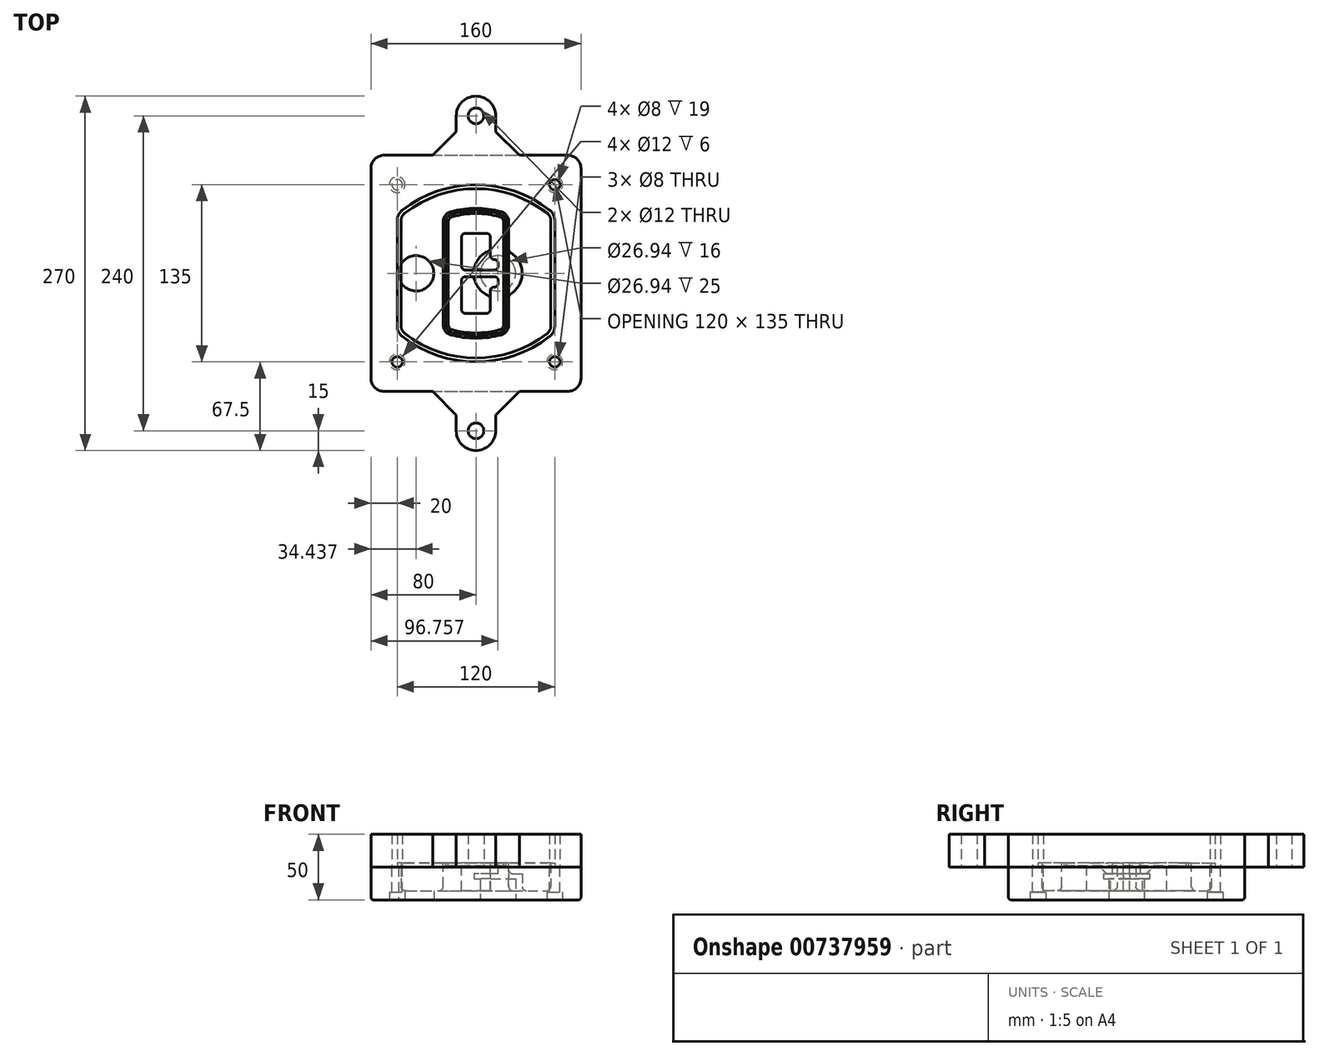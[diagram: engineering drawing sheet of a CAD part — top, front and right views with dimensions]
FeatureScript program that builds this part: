
annotation { "Feature Type Name" : "Feature", "Feature Type Description" : "" }
export const myFeature = defineFeature(function(context is Context, id is Id, definition is map)
    precondition{}
    {
        {
            var Q0;
            Q0=qCreatedBy(makeId("Top.planeOp"),FACE);
            var sketch = newSketch(context, id + "F0", { "sketchPlane" : qUnion([Q0])});
            skPoint(sketch, "E0.rect.middle", {"position": v(0, 0) * mm});
            skLineSegment(sketch, "E1.bottom", {"start": v(-70, -90) * mm, "end": v(70, -90) * mm});
            skLineSegment(sketch, "E1.top", {"start": v(-70, 90) * mm, "end": v(70, 90) * mm});
            skLineSegment(sketch, "E1.left", {"start": v(-80, -80) * mm, "end": v(-80, 80) * mm});
            skLineSegment(sketch, "E1.right", {"start": v(80, -80) * mm, "end": v(80, 80) * mm});
            skLineSegment(sketch, "E2", {"start": v(-80, 90) * mm, "end": v(80, -90) * mm, "construction": true});
            skLineSegment(sketch, "E3", {"start": v(80, 90) * mm, "end": v(-80, -90) * mm, "construction": true});
            skCircle(sketch, "E4", {"center": v(-60, 67.5) * mm, "radius": 4 * mm});
            skCircle(sketch, "E5", {"center": v(60, 67.5) * mm, "radius": 4 * mm});
            skCircle(sketch, "E6", {"center": v(60, -67.5) * mm, "radius": 4 * mm});
            skCircle(sketch, "E7", {"center": v(-60, -67.5) * mm, "radius": 4 * mm});
            skLineSegment(sketch, "E8", {"start": v(-60, 67.5) * mm, "end": v(60, 67.5) * mm, "construction": true});
            skLineSegment(sketch, "E9", {"start": v(60, 67.5) * mm, "end": v(60, -67.5) * mm, "construction": true});
            skLineSegment(sketch, "E10", {"start": v(60, -67.5) * mm, "end": v(-60, -67.5) * mm, "construction": true});
            skLineSegment(sketch, "E11", {"start": v(-60, -67.5) * mm, "end": v(-60, 67.5) * mm, "construction": true});
            skLineSegment(sketch, "E12", {"start": v(-60, 40.3) * mm, "end": v(-60, -40.3) * mm});
            skLineSegment(sketch, "E13", {"start": v(60, 40.3) * mm, "end": v(60, -40.3) * mm});
            skArc(sketch, "E14", {"start": v(56.15, 48.18) * mm, "mid": v(0, 67.5) * mm, "end": v(-56.15, 48.18) * mm});
            skArc(sketch, "E15", {"start": v(-56.15, -48.18) * mm, "mid": v(0, -67.5) * mm, "end": v(56.15, -48.18) * mm});
            skLineSegment(sketch, "E16", {"start": v(-60, 0) * mm, "end": v(60, 0) * mm, "construction": true});
            skPoint(sketch, "E17.visualSharp", {"position": v(-60, -45) * mm});
            skArc(sketch, "E17.filletArc", {"start": v(-60, -40.3) * mm, "mid": v(-58.99, -44.68) * mm, "end": v(-56.15, -48.18) * mm});
            skPoint(sketch, "E18.visualSharp", {"position": v(-60, 45) * mm});
            skArc(sketch, "E18.filletArc", {"start": v(-56.15, 48.18) * mm, "mid": v(-58.99, 44.68) * mm, "end": v(-60, 40.3) * mm});
            skPoint(sketch, "E19.visualSharp", {"position": v(60, 45) * mm});
            skArc(sketch, "E19.filletArc", {"start": v(60, 40.3) * mm, "mid": v(58.99, 44.68) * mm, "end": v(56.15, 48.18) * mm});
            skPoint(sketch, "E20.visualSharp", {"position": v(60, -45) * mm});
            skArc(sketch, "E20.filletArc", {"start": v(56.15, -48.18) * mm, "mid": v(58.99, -44.68) * mm, "end": v(60, -40.3) * mm});
            skPoint(sketch, "E21.visualSharp", {"position": v(-80, 90) * mm});
            skArc(sketch, "E21.filletArc", {"start": v(-70, 90) * mm, "mid": v(-77.07, 87.07) * mm, "end": v(-80, 80) * mm});
            skPoint(sketch, "E22.visualSharp", {"position": v(80, 90) * mm});
            skArc(sketch, "E22.filletArc", {"start": v(80, 80) * mm, "mid": v(77.07, 87.07) * mm, "end": v(70, 90) * mm});
            skPoint(sketch, "E23.visualSharp", {"position": v(80, -90) * mm});
            skArc(sketch, "E23.filletArc", {"start": v(70, -90) * mm, "mid": v(77.07, -87.07) * mm, "end": v(80, -80) * mm});
            skPoint(sketch, "E24.visualSharp", {"position": v(-80, -90) * mm});
            skArc(sketch, "E24.filletArc", {"start": v(-80, -80) * mm, "mid": v(-77.07, -87.07) * mm, "end": v(-70, -90) * mm});
            skArc(sketch, "E25.0", {"start": v(57, 40.3) * mm, "mid": v(56.3, 43.36) * mm, "end": v(54.3, 45.81) * mm});
            skLineSegment(sketch, "E25.1", {"start": v(57, 40.3) * mm, "end": v(57, -40.3) * mm});
            skArc(sketch, "E25.2", {"start": v(54.3, -45.81) * mm, "mid": v(56.3, -43.36) * mm, "end": v(57, -40.3) * mm});
            skArc(sketch, "E25.3", {"start": v(-54.3, -45.81) * mm, "mid": v(0, -64.5) * mm, "end": v(54.3, -45.81) * mm});
            skArc(sketch, "E25.4", {"start": v(-57, -40.3) * mm, "mid": v(-56.3, -43.36) * mm, "end": v(-54.3, -45.81) * mm});
            skArc(sketch, "E25.5", {"start": v(54.3, 45.81) * mm, "mid": v(0, 64.5) * mm, "end": v(-54.3, 45.81) * mm});
            skLineSegment(sketch, "E25.6", {"start": v(-57, 40.3) * mm, "end": v(-57, -40.3) * mm});
            skArc(sketch, "E25.7", {"start": v(-54.3, 45.81) * mm, "mid": v(-56.3, 43.36) * mm, "end": v(-57, 40.3) * mm});
            skArc(sketch, "E26.0", {"start": v(-58.62, 51.33) * mm, "mid": v(-62.58, 46.43) * mm, "end": v(-64, 40.3) * mm});
            skArc(sketch, "E26.1", {"start": v(58.62, 51.33) * mm, "mid": v(0, 71.5) * mm, "end": v(-58.62, 51.33) * mm});
            skArc(sketch, "E26.2", {"start": v(64, 40.3) * mm, "mid": v(62.58, 46.43) * mm, "end": v(58.62, 51.33) * mm});
            skLineSegment(sketch, "E26.3", {"start": v(64, 40.3) * mm, "end": v(64, -40.3) * mm});
            skArc(sketch, "E26.4", {"start": v(58.62, -51.33) * mm, "mid": v(62.58, -46.43) * mm, "end": v(64, -40.3) * mm});
            skLineSegment(sketch, "E26.5", {"start": v(-64, 40.3) * mm, "end": v(-64, -40.3) * mm});
            skArc(sketch, "E26.6", {"start": v(-58.62, -51.33) * mm, "mid": v(0, -71.5) * mm, "end": v(58.62, -51.33) * mm});
            skArc(sketch, "E26.7", {"start": v(-64, -40.3) * mm, "mid": v(-62.58, -46.43) * mm, "end": v(-58.62, -51.33) * mm});
            skSolve(sketch);
        }
        {
            var Q0;
            Q0=makeQuery(id+"F0.imprint","IMPRINT",FACE,{"disambiguationData":[TD([[makeQuery(id+"F0.imprint","IMPRINT",EDGE,{"derivedFrom":sQuery(id+"F0.wireOp",EDGE,"E1.bottom")}),1.0]])]});
            var Q1;
            Q1=makeQuery(id+"F0.imprint","IMPRINT",FACE,{"disambiguationData":[TD([[makeQuery(id+"F0.imprint","IMPRINT",EDGE,{"derivedFrom":sQuery(id+"F0.wireOp",EDGE,"E12")}),1.0]])]});
            var Q2;
            Q2=makeQuery(id+"F0.imprint","IMPRINT",FACE,{"disambiguationData":[TD([[makeQuery(id+"F0.imprint","IMPRINT",EDGE,{"derivedFrom":sQuery(id+"F0.wireOp",EDGE,"E25.0")}),1.0]])]});
            var Q3;
            Q3=makeQuery(id+"F0.imprint","IMPRINT",FACE,{"disambiguationData":[TD([[makeQuery(id+"F0.imprint","IMPRINT",EDGE,{"derivedFrom":sQuery(id+"F0.wireOp",EDGE,"E12")}),-1.0]])]});
            extrude(context, id + "F1", {"entities" : qUnion([Q0, Q1, Q2, Q3]), "oppositeDirection" : true, "depth" : 25 * mm});
        }
        {
            var Q0;
            Q0=makeQuery(id+"F0.imprint","IMPRINT",FACE,{"disambiguationData":[TD([[makeQuery(id+"F0.imprint","IMPRINT",EDGE,{"derivedFrom":sQuery(id+"F0.wireOp",EDGE,"E12")}),1.0]])]});
            extrude(context, id + "F2", {"entities" : qUnion([Q0]), "operationType" : NewBodyOperationType.ADD, "depth" : 3 * mm});
        }
        {
            var Q0;
            Q0=makeQuery(id+"F0.imprint","IMPRINT",FACE,{"disambiguationData":[TD([[makeQuery(id+"F0.imprint","IMPRINT",EDGE,{"derivedFrom":sQuery(id+"F0.wireOp",EDGE,"E25.0")}),1.0]])]});
            extrude(context, id + "F3", {"entities" : qUnion([Q0]), "operationType" : NewBodyOperationType.REMOVE, "oppositeDirection" : true, "depth" : 18 * mm});
        }
        {
            var Q0;
            Q0=makeQuery(id+"F2.opExtrude","CAP_FACE",FACE,{"disambiguationData":[OSD([sQuery(id+"F0.wireOp",EDGE,"E12"),sQuery(id+"F0.wireOp",EDGE,"E13"),sQuery(id+"F0.wireOp",EDGE,"E14"),sQuery(id+"F0.wireOp",EDGE,"E15"),sQuery(id+"F0.wireOp",EDGE,"E17.filletArc"),sQuery(id+"F0.wireOp",EDGE,"E18.filletArc"),sQuery(id+"F0.wireOp",EDGE,"E19.filletArc"),sQuery(id+"F0.wireOp",EDGE,"E20.filletArc"),sQuery(id+"F0.wireOp",EDGE,"E25.0"),sQuery(id+"F0.wireOp",EDGE,"E25.1"),sQuery(id+"F0.wireOp",EDGE,"E25.2"),sQuery(id+"F0.wireOp",EDGE,"E25.3"),sQuery(id+"F0.wireOp",EDGE,"E25.4"),sQuery(id+"F0.wireOp",EDGE,"E25.5"),sQuery(id+"F0.wireOp",EDGE,"E25.6"),sQuery(id+"F0.wireOp",EDGE,"E25.7")])],"isStart":false});
            var sketch = newSketch(context, id + "F4", { "sketchPlane" : qUnion([Q0])});
            skArc(sketch, "E27.0", {"start": v(-19.08, -46.97) * mm, "mid": v(0, -49.5) * mm, "end": v(19.08, -46.97) * mm});
            skArc(sketch, "E28.0", {"start": v(19.08, 46.97) * mm, "mid": v(0, 49.5) * mm, "end": v(-19.08, 46.97) * mm});
            skLineSegment(sketch, "E29", {"start": v(-25, 39.25) * mm, "end": v(-25, -39.25) * mm});
            skLineSegment(sketch, "E30", {"start": v(25, 39.25) * mm, "end": v(25, -39.25) * mm});
            skLineSegment(sketch, "E31", {"start": v(-25, 45.1) * mm, "end": v(25, 45.1) * mm, "construction": true});
            skLineSegment(sketch, "E32", {"start": v(-25, -45.1) * mm, "end": v(25, -45.1) * mm, "construction": true});
            skPoint(sketch, "E33.visualSharp", {"position": v(-25, 45.1) * mm});
            skArc(sketch, "E33.filletArc", {"start": v(-19.08, 46.97) * mm, "mid": v(-23.35, 44.11) * mm, "end": v(-25, 39.25) * mm});
            skPoint(sketch, "E34.visualSharp", {"position": v(25, 45.1) * mm});
            skArc(sketch, "E34.filletArc", {"start": v(25, 39.25) * mm, "mid": v(23.35, 44.11) * mm, "end": v(19.08, 46.97) * mm});
            skPoint(sketch, "E35.visualSharp", {"position": v(25, -45.1) * mm});
            skArc(sketch, "E35.filletArc", {"start": v(19.08, -46.97) * mm, "mid": v(23.35, -44.11) * mm, "end": v(25, -39.25) * mm});
            skPoint(sketch, "E36.visualSharp", {"position": v(-25, -45.1) * mm});
            skArc(sketch, "E36.filletArc", {"start": v(-25, -39.25) * mm, "mid": v(-23.35, -44.11) * mm, "end": v(-19.08, -46.97) * mm});
            skArc(sketch, "E37.0", {"start": v(54.3, 45.81) * mm, "mid": v(0, 64.5) * mm, "end": v(-54.3, 45.81) * mm});
            skArc(sketch, "E37.1", {"start": v(-54.3, 45.81) * mm, "mid": v(-56.3, 43.36) * mm, "end": v(-57, 40.3) * mm});
            skLineSegment(sketch, "E37.2", {"start": v(-57, 40.3) * mm, "end": v(-57, -40.3) * mm});
            skArc(sketch, "E37.3", {"start": v(-57, -40.3) * mm, "mid": v(-56.3, -43.36) * mm, "end": v(-54.3, -45.81) * mm});
            skArc(sketch, "E37.4", {"start": v(-54.3, -45.81) * mm, "mid": v(0, -64.5) * mm, "end": v(54.3, -45.81) * mm});
            skArc(sketch, "E37.5", {"start": v(54.3, -45.81) * mm, "mid": v(56.3, -43.36) * mm, "end": v(57, -40.3) * mm});
            skLineSegment(sketch, "E37.6", {"start": v(57, 40.3) * mm, "end": v(57, -40.3) * mm});
            skArc(sketch, "E37.7", {"start": v(57, 40.3) * mm, "mid": v(56.3, 43.36) * mm, "end": v(54.3, 45.81) * mm});
            skLineSegment(sketch, "E38.0", {"start": v(23, 39.25) * mm, "end": v(23, -39.25) * mm});
            skArc(sketch, "E38.1", {"start": v(18.56, -45.04) * mm, "mid": v(21.76, -42.9) * mm, "end": v(23, -39.25) * mm});
            skArc(sketch, "E38.2", {"start": v(-18.56, -45.04) * mm, "mid": v(0, -47.5) * mm, "end": v(18.56, -45.04) * mm});
            skArc(sketch, "E38.3", {"start": v(-23, -39.25) * mm, "mid": v(-21.76, -42.9) * mm, "end": v(-18.56, -45.04) * mm});
            skLineSegment(sketch, "E38.4", {"start": v(-23, 39.25) * mm, "end": v(-23, -39.25) * mm});
            skArc(sketch, "E38.5", {"start": v(23, 39.25) * mm, "mid": v(21.76, 42.9) * mm, "end": v(18.56, 45.04) * mm});
            skArc(sketch, "E38.6", {"start": v(-18.56, 45.04) * mm, "mid": v(-21.76, 42.9) * mm, "end": v(-23, 39.25) * mm});
            skArc(sketch, "E38.7", {"start": v(18.56, 45.04) * mm, "mid": v(0, 47.5) * mm, "end": v(-18.56, 45.04) * mm});
            skArc(sketch, "E39.0", {"start": v(21, 39.25) * mm, "mid": v(20.18, 41.68) * mm, "end": v(18.04, 43.1) * mm});
            skLineSegment(sketch, "E39.1", {"start": v(21, 39.25) * mm, "end": v(21, -39.25) * mm});
            skArc(sketch, "E39.2", {"start": v(18.04, -43.1) * mm, "mid": v(20.18, -41.68) * mm, "end": v(21, -39.25) * mm});
            skArc(sketch, "E39.3", {"start": v(-18.04, -43.1) * mm, "mid": v(0, -45.5) * mm, "end": v(18.04, -43.1) * mm});
            skArc(sketch, "E39.4", {"start": v(-21, -39.25) * mm, "mid": v(-20.18, -41.68) * mm, "end": v(-18.04, -43.1) * mm});
            skArc(sketch, "E39.5", {"start": v(18.04, 43.1) * mm, "mid": v(0, 45.5) * mm, "end": v(-18.04, 43.1) * mm});
            skLineSegment(sketch, "E39.6", {"start": v(-21, 39.25) * mm, "end": v(-21, -39.25) * mm});
            skArc(sketch, "E39.7", {"start": v(-18.04, 43.1) * mm, "mid": v(-20.18, 41.68) * mm, "end": v(-21, 39.25) * mm});
            skLineSegment(sketch, "E40", {"start": v(-25, 0) * mm, "end": v(25, 0) * mm, "construction": true});
            skLineSegment(sketch, "E41", {"start": v(-11, 5.5) * mm, "end": v(-11, 27.5) * mm});
            skLineSegment(sketch, "E42", {"start": v(-8, 30.5) * mm, "end": v(8, 30.5) * mm});
            skLineSegment(sketch, "E43", {"start": v(11, 27.5) * mm, "end": v(11, 13.5) * mm});
            skLineSegment(sketch, "E44", {"start": v(14, 10.5) * mm, "end": v(14, 10.5) * mm});
            skLineSegment(sketch, "E45", {"start": v(17, 7.5) * mm, "end": v(17, 5.5) * mm});
            skLineSegment(sketch, "E46", {"start": v(14, 2.5) * mm, "end": v(-8, 2.5) * mm});
            skPoint(sketch, "E47.visualSharp", {"position": v(-11, 30.5) * mm});
            skArc(sketch, "E47.filletArc", {"start": v(-8, 30.5) * mm, "mid": v(-10.12, 29.62) * mm, "end": v(-11, 27.5) * mm});
            skPoint(sketch, "E48.visualSharp", {"position": v(11, 30.5) * mm});
            skArc(sketch, "E48.filletArc", {"start": v(11, 27.5) * mm, "mid": v(10.12, 29.62) * mm, "end": v(8, 30.5) * mm});
            skPoint(sketch, "E49.visualSharp", {"position": v(11, 10.5) * mm});
            skArc(sketch, "E49.filletArc", {"start": v(11, 13.5) * mm, "mid": v(11.88, 11.38) * mm, "end": v(14, 10.5) * mm});
            skPoint(sketch, "E50.visualSharp", {"position": v(17, 10.5) * mm});
            skArc(sketch, "E50.filletArc", {"start": v(17, 7.5) * mm, "mid": v(16.12, 9.62) * mm, "end": v(14, 10.5) * mm});
            skPoint(sketch, "E51.visualSharp", {"position": v(17, 2.5) * mm});
            skArc(sketch, "E51.filletArc", {"start": v(14, 2.5) * mm, "mid": v(16.12, 3.38) * mm, "end": v(17, 5.5) * mm});
            skPoint(sketch, "E52.visualSharp", {"position": v(-11, 2.5) * mm});
            skArc(sketch, "E52.filletArc", {"start": v(-11, 5.5) * mm, "mid": v(-10.12, 3.38) * mm, "end": v(-8, 2.5) * mm});
            skLineSegment(sketch, "E53.0.MirrorCS", {"start": v(14, -2.5) * mm, "end": v(-8, -2.5) * mm});
            skArc(sketch, "E54.0.MirrorCS", {"start": v(-11, -5.5) * mm, "mid": v(-10.12, -3.38) * mm, "end": v(-8, -2.5) * mm});
            skLineSegment(sketch, "E55.0.MirrorCS", {"start": v(-11, -5.5) * mm, "end": v(-11, -27.5) * mm});
            skArc(sketch, "E56.0.MirrorCS", {"start": v(-8, -30.5) * mm, "mid": v(-10.12, -29.62) * mm, "end": v(-11, -27.5) * mm});
            skLineSegment(sketch, "E57.0.MirrorCS", {"start": v(-8, -30.5) * mm, "end": v(8, -30.5) * mm});
            skArc(sketch, "E58.0.MirrorCS", {"start": v(11, -27.5) * mm, "mid": v(10.12, -29.62) * mm, "end": v(8, -30.5) * mm});
            skLineSegment(sketch, "E59.0.MirrorCS", {"start": v(11, -27.5) * mm, "end": v(11, -13.5) * mm});
            skArc(sketch, "E60.0.MirrorCS", {"start": v(11, -13.5) * mm, "mid": v(11.88, -11.38) * mm, "end": v(14, -10.5) * mm});
            skArc(sketch, "E61.0.MirrorCS", {"start": v(17, -7.5) * mm, "mid": v(16.12, -9.62) * mm, "end": v(14, -10.5) * mm});
            skLineSegment(sketch, "E62.0.MirrorCS", {"start": v(17, -7.5) * mm, "end": v(17, -5.5) * mm});
            skArc(sketch, "E63.0.MirrorCS", {"start": v(14, -2.5) * mm, "mid": v(16.12, -3.38) * mm, "end": v(17, -5.5) * mm});
            skSolve(sketch);
        }
        {
            var Q0;
            Q0=makeQuery(id+"F4.imprint","IMPRINT",FACE,{"disambiguationData":[TD([[makeQuery(id+"F4.imprint","IMPRINT",EDGE,{"derivedFrom":sQuery(id+"F4.wireOp",EDGE,"E27.0")}),1.0]])]});
            var Q1;
            Q1=makeQuery(id+"F4.imprint","IMPRINT",FACE,{"disambiguationData":[TD([[makeQuery(id+"F4.imprint","IMPRINT",EDGE,{"derivedFrom":sQuery(id+"F4.wireOp",EDGE,"E38.0")}),-1.0]])]});
            var Q2;
            Q2=makeQuery(id+"F4.imprint","IMPRINT",FACE,{"disambiguationData":[TD([[makeQuery(id+"F4.imprint","IMPRINT",EDGE,{"derivedFrom":sQuery(id+"F4.wireOp",EDGE,"E39.0")}),1.0]])]});
            extrude(context, id + "F5", {"entities" : qUnion([Q0, Q1, Q2]), "operationType" : NewBodyOperationType.ADD, "endBound" : BoundingType.UP_TO_NEXT, "oppositeDirection" : true, "depth" : 25 * mm});
        }
        {
            var Q0;
            Q0=makeQuery(id+"F4.imprint","IMPRINT",FACE,{"disambiguationData":[TD([[makeQuery(id+"F4.imprint","IMPRINT",EDGE,{"derivedFrom":sQuery(id+"F4.wireOp",EDGE,"E38.0")}),-1.0]])]});
            extrude(context, id + "F6", {"entities" : qUnion([Q0]), "operationType" : NewBodyOperationType.REMOVE, "oppositeDirection" : true, "depth" : 2 * mm});
        }
        {
            var Q0;
            Q0=makeQuery(id+"F1.opExtrude","CAP_FACE",FACE,{"disambiguationData":[OSD([sQuery(id+"F0.wireOp",EDGE,"E1.bottom"),sQuery(id+"F0.wireOp",EDGE,"E1.top"),sQuery(id+"F0.wireOp",EDGE,"E1.left"),sQuery(id+"F0.wireOp",EDGE,"E1.right"),sQuery(id+"F0.wireOp",EDGE,"E4"),sQuery(id+"F0.wireOp",EDGE,"E5"),sQuery(id+"F0.wireOp",EDGE,"E6"),sQuery(id+"F0.wireOp",EDGE,"E7"),sQuery(id+"F0.wireOp",EDGE,"E21.filletArc"),sQuery(id+"F0.wireOp",EDGE,"E22.filletArc"),sQuery(id+"F0.wireOp",EDGE,"E23.filletArc"),sQuery(id+"F0.wireOp",EDGE,"E24.filletArc")])],"isStart":false});
            var sketch = newSketch(context, id + "F7", { "sketchPlane" : qUnion([Q0])});
            skCircle(sketch, "E64", {"center": v(16.76, 0) * mm, "radius": 13.47 * mm});
            skCircle(sketch, "E65", {"center": v(-45.56, 0) * mm, "radius": 13.47 * mm});
            skLineSegment(sketch, "E66", {"start": v(80, 0) * mm, "end": v(-80, 0) * mm});
            skCircle(sketch, "E67", {"center": v(16.76, 0) * mm, "radius": 18.47 * mm});
            skCircle(sketch, "E68", {"center": v(60, -67.5) * mm, "radius": 6 * mm});
            skCircle(sketch, "E69", {"center": v(-60, -67.5) * mm, "radius": 6 * mm});
            skCircle(sketch, "E70", {"center": v(-60, 67.5) * mm, "radius": 6 * mm});
            skCircle(sketch, "E71", {"center": v(60, 67.5) * mm, "radius": 6 * mm});
            skSolve(sketch);
        }
        {
            var Q0;
            {var subQ1=sQuery(id+"F7.wireOp",EDGE,"E66");var subQ4=sQuery(id+"F7.wireOp",EDGE,"E64");var subQ6=makeQuery(id+"F7.imprint","INTERSECT",VERTEX,{"disambiguationData":[OD(0.0)],"derivedFrom":[subQ4,subQ1]});Q0=makeQuery(id+"F7.imprint","IMPRINT",FACE,{"disambiguationData":[TD([[makeQuery(id+"F7.imprint","IMPRINT",EDGE,{"disambiguationData":[TD([[subQ6,-1.0]])],"derivedFrom":subQ4}),-1.0]])]});}
            var Q1;
            {var subQ0=sQuery(id+"F7.wireOp",EDGE,"E66");var subQ1=sQuery(id+"F7.wireOp",EDGE,"E64");var subQ3=makeQuery(id+"F7.imprint","INTERSECT",VERTEX,{"disambiguationData":[OD(0.0)],"derivedFrom":[subQ1,subQ0]});Q1=makeQuery(id+"F7.imprint","IMPRINT",FACE,{"disambiguationData":[TD([[makeQuery(id+"F7.imprint","IMPRINT",EDGE,{"disambiguationData":[TD([[subQ3,-1.0]])],"derivedFrom":subQ1}),1.0]])]});}
            var Q2;
            {var subQ0=sQuery(id+"F7.wireOp",EDGE,"E66");var subQ1=sQuery(id+"F7.wireOp",EDGE,"E64");var subQ3=makeQuery(id+"F7.imprint","INTERSECT",VERTEX,{"disambiguationData":[OD(0.0)],"derivedFrom":[subQ1,subQ0]});Q2=makeQuery(id+"F7.imprint","IMPRINT",FACE,{"disambiguationData":[TD([[makeQuery(id+"F7.imprint","IMPRINT",EDGE,{"disambiguationData":[TD([[subQ3,1.0]])],"derivedFrom":subQ1}),1.0]])]});}
            var Q3;
            {var subQ1=sQuery(id+"F7.wireOp",EDGE,"E66");var subQ4=sQuery(id+"F7.wireOp",EDGE,"E64");var subQ6=makeQuery(id+"F7.imprint","INTERSECT",VERTEX,{"disambiguationData":[OD(0.0)],"derivedFrom":[subQ4,subQ1]});Q3=makeQuery(id+"F7.imprint","IMPRINT",FACE,{"disambiguationData":[TD([[makeQuery(id+"F7.imprint","IMPRINT",EDGE,{"disambiguationData":[TD([[subQ6,1.0]])],"derivedFrom":subQ4}),-1.0]])]});}
            extrude(context, id + "F8", {"entities" : qUnion([Q0, Q1, Q2, Q3]), "operationType" : NewBodyOperationType.ADD, "oppositeDirection" : true, "depth" : 20 * mm});
        }
        {
            var Q0;
            {var subQ0=sQuery(id+"F7.wireOp",EDGE,"E66");var subQ1=sQuery(id+"F7.wireOp",EDGE,"E64");var subQ3=makeQuery(id+"F7.imprint","INTERSECT",VERTEX,{"disambiguationData":[OD(0.0)],"derivedFrom":[subQ1,subQ0]});Q0=makeQuery(id+"F7.imprint","IMPRINT",FACE,{"disambiguationData":[TD([[makeQuery(id+"F7.imprint","IMPRINT",EDGE,{"disambiguationData":[TD([[subQ3,-1.0]])],"derivedFrom":subQ1}),1.0]])]});}
            var Q1;
            {var subQ0=sQuery(id+"F7.wireOp",EDGE,"E66");var subQ1=sQuery(id+"F7.wireOp",EDGE,"E64");var subQ3=makeQuery(id+"F7.imprint","INTERSECT",VERTEX,{"disambiguationData":[OD(0.0)],"derivedFrom":[subQ1,subQ0]});Q1=makeQuery(id+"F7.imprint","IMPRINT",FACE,{"disambiguationData":[TD([[makeQuery(id+"F7.imprint","IMPRINT",EDGE,{"disambiguationData":[TD([[subQ3,1.0]])],"derivedFrom":subQ1}),1.0]])]});}
            extrude(context, id + "F9", {"entities" : qUnion([Q0, Q1]), "operationType" : NewBodyOperationType.REMOVE, "oppositeDirection" : true, "depth" : 16 * mm});
        }
        {
            var Q0;
            {var subQ0=sQuery(id+"F7.wireOp",EDGE,"E66");var subQ1=sQuery(id+"F7.wireOp",EDGE,"E65");var subQ3=makeQuery(id+"F7.imprint","INTERSECT",VERTEX,{"disambiguationData":[OD(0.0)],"derivedFrom":[subQ1,subQ0]});Q0=makeQuery(id+"F7.imprint","IMPRINT",FACE,{"disambiguationData":[TD([[makeQuery(id+"F7.imprint","IMPRINT",EDGE,{"disambiguationData":[TD([[subQ3,-1.0]])],"derivedFrom":subQ1}),1.0]])]});}
            var Q1;
            {var subQ0=sQuery(id+"F7.wireOp",EDGE,"E66");var subQ1=sQuery(id+"F7.wireOp",EDGE,"E65");var subQ3=makeQuery(id+"F7.imprint","INTERSECT",VERTEX,{"disambiguationData":[OD(0.0)],"derivedFrom":[subQ1,subQ0]});Q1=makeQuery(id+"F7.imprint","IMPRINT",FACE,{"disambiguationData":[TD([[makeQuery(id+"F7.imprint","IMPRINT",EDGE,{"disambiguationData":[TD([[subQ3,1.0]])],"derivedFrom":subQ1}),1.0]])]});}
            extrude(context, id + "F10", {"entities" : qUnion([Q0, Q1]), "operationType" : NewBodyOperationType.REMOVE, "oppositeDirection" : true, "depth" : 25 * mm});
        }
        {
            var Q0;
            Q0=makeQuery(id+"F7.imprint","IMPRINT",FACE,{"disambiguationData":[TD([[makeQuery(id+"F7.imprint","IMPRINT",EDGE,{"derivedFrom":sQuery(id+"F7.wireOp",EDGE,"E68")}),1.0]])]});
            var Q1;
            Q1=makeQuery(id+"F7.imprint","IMPRINT",FACE,{"disambiguationData":[TD([[makeQuery(id+"F7.imprint","IMPRINT",EDGE,{"derivedFrom":makeQuery(id+"F1.opExtrude","CAP_EDGE",EDGE,{"disambiguationData":[OSD([sQuery(id+"F0.wireOp",EDGE,"E5")])],"isStart":false})}),-1.0]])]});
            var Q2;
            Q2=makeQuery(id+"F7.imprint","IMPRINT",FACE,{"disambiguationData":[TD([[makeQuery(id+"F7.imprint","IMPRINT",EDGE,{"derivedFrom":sQuery(id+"F7.wireOp",EDGE,"E69")}),1.0]])]});
            var Q3;
            Q3=makeQuery(id+"F7.imprint","IMPRINT",FACE,{"disambiguationData":[TD([[makeQuery(id+"F7.imprint","IMPRINT",EDGE,{"derivedFrom":makeQuery(id+"F1.opExtrude","CAP_EDGE",EDGE,{"disambiguationData":[OSD([sQuery(id+"F0.wireOp",EDGE,"E4")])],"isStart":false})}),-1.0]])]});
            var Q4;
            Q4=makeQuery(id+"F7.imprint","IMPRINT",FACE,{"disambiguationData":[TD([[makeQuery(id+"F7.imprint","IMPRINT",EDGE,{"derivedFrom":sQuery(id+"F7.wireOp",EDGE,"E70")}),1.0]])]});
            var Q5;
            Q5=makeQuery(id+"F7.imprint","IMPRINT",FACE,{"disambiguationData":[TD([[makeQuery(id+"F7.imprint","IMPRINT",EDGE,{"derivedFrom":makeQuery(id+"F1.opExtrude","CAP_EDGE",EDGE,{"disambiguationData":[OSD([sQuery(id+"F0.wireOp",EDGE,"E7")])],"isStart":false})}),-1.0]])]});
            var Q6;
            Q6=makeQuery(id+"F7.imprint","IMPRINT",FACE,{"disambiguationData":[TD([[makeQuery(id+"F7.imprint","IMPRINT",EDGE,{"derivedFrom":sQuery(id+"F7.wireOp",EDGE,"E71")}),1.0]])]});
            var Q7;
            Q7=makeQuery(id+"F7.imprint","IMPRINT",FACE,{"disambiguationData":[TD([[makeQuery(id+"F7.imprint","IMPRINT",EDGE,{"derivedFrom":makeQuery(id+"F1.opExtrude","CAP_EDGE",EDGE,{"disambiguationData":[OSD([sQuery(id+"F0.wireOp",EDGE,"E6")])],"isStart":false})}),-1.0]])]});
            extrude(context, id + "F11", {"entities" : qUnion([Q0, Q1, Q2, Q3, Q4, Q5, Q6, Q7]), "operationType" : NewBodyOperationType.REMOVE, "oppositeDirection" : true, "depth" : 6 * mm});
        }
        {
            var Q0;
            Q0=makeQuery(id+"F9.boolean.opBoolean","COPY",FACE,{"derivedFrom":makeQuery(id+"F9.opExtrude","CAP_FACE",FACE,{"disambiguationData":[OSD([sQuery(id+"F7.wireOp",EDGE,"E64")])],"isStart":false})});
            var sketch = newSketch(context, id + "F12", { "sketchPlane" : qUnion([Q0])});
            skArc(sketch, "E72.0", {"start": v(11, 17.55) * mm, "mid": v(2.57, 11.82) * mm, "end": v(-1.54, 2.5) * mm});
            skArc(sketch, "E72.1", {"start": v(-1.54, -2.5) * mm, "mid": v(2.57, -11.82) * mm, "end": v(11, -17.55) * mm});
            skLineSegment(sketch, "E73", {"start": v(-1.54, -2.5) * mm, "end": v(14, -2.5) * mm});
            skLineSegment(sketch, "E74.0", {"start": v(14, 2.5) * mm, "end": v(-1.54, 2.5) * mm});
            skArc(sketch, "E74.1", {"start": v(14, 2.5) * mm, "mid": v(16.12, 3.38) * mm, "end": v(17, 5.5) * mm});
            skLineSegment(sketch, "E74.2", {"start": v(17, 7.5) * mm, "end": v(17, 5.5) * mm});
            skArc(sketch, "E74.3", {"start": v(17, 7.5) * mm, "mid": v(16.12, 9.62) * mm, "end": v(14, 10.5) * mm});
            skArc(sketch, "E74.4", {"start": v(11, 13.5) * mm, "mid": v(11.88, 11.38) * mm, "end": v(14, 10.5) * mm});
            skLineSegment(sketch, "E74.5", {"start": v(11, 17.55) * mm, "end": v(11, 13.5) * mm});
            skLineSegment(sketch, "E74.7", {"start": v(14, -2.5) * mm, "end": v(-1.54, -2.5) * mm});
            skArc(sketch, "E74.8", {"start": v(14, -2.5) * mm, "mid": v(16.12, -3.38) * mm, "end": v(17, -5.5) * mm});
            skLineSegment(sketch, "E74.9", {"start": v(17, -7.5) * mm, "end": v(17, -5.5) * mm});
            skArc(sketch, "E74.10", {"start": v(17, -7.5) * mm, "mid": v(16.12, -9.62) * mm, "end": v(14, -10.5) * mm});
            skArc(sketch, "E74.11", {"start": v(11, -13.5) * mm, "mid": v(11.88, -11.38) * mm, "end": v(14, -10.5) * mm});
            skLineSegment(sketch, "E74.12", {"start": v(11, -17.55) * mm, "end": v(11, -13.5) * mm});
            skPoint(sketch, "E75.orphan", {"position": v(11, -27.5) * mm});
            skPoint(sketch, "E76.orphan", {"position": v(-8, -2.5) * mm});
            skPoint(sketch, "E77.orphan", {"position": v(-8, 2.5) * mm});
            skPoint(sketch, "E78.orphan", {"position": v(11, 27.5) * mm});
            skSolve(sketch);
        }
        {
            var Q0;
            {var subQ7=sQuery(id+"F12.wireOp",EDGE,"E72.0");var subQ14=sQuery(id+"F12.wireOp",EDGE,"E72.1");var subQ16=sQuery(id+"F12.wireOp",EDGE,"E74.1");var subQ18=sQuery(id+"F12.wireOp",EDGE,"E74.8");Q0=qUnion([makeQuery(id+"F12.imprint","IMPRINT",FACE,{"disambiguationData":[TD([[makeQuery(id+"F12.imprint","IMPRINT",EDGE,{"derivedFrom":subQ7}),1.0]])]}),makeQuery(id+"F12.imprint","IMPRINT",FACE,{"disambiguationData":[TD([[makeQuery(id+"F12.imprint","IMPRINT",EDGE,{"derivedFrom":subQ14}),1.0]])]}),makeQuery(id+"F12.imprint","IMPRINT",FACE,{"disambiguationData":[TD([[makeQuery(id+"F12.imprint","IMPRINT",EDGE,{"derivedFrom":subQ16}),1.0]])]}),makeQuery(id+"F12.imprint","IMPRINT",FACE,{"disambiguationData":[TD([[makeQuery(id+"F12.imprint","IMPRINT",EDGE,{"derivedFrom":subQ18}),-1.0]])]})]);}
            var Q1;
            Q1=makeQuery(id+"F5.boolean.opBoolean","SPLIT",FACE,{"disambiguationData":[TD([makeQuery(id+"F5.opExtrude","SWEPT_FACE",FACE,{"disambiguationData":[OSD([sQuery(id+"F4.wireOp",EDGE,"E41")])]})])],"derivedFrom":makeQuery(id+"F3.boolean.opBoolean","COPY",FACE,{"derivedFrom":makeQuery(id+"F3.opExtrude","CAP_FACE",FACE,{"disambiguationData":[OSD([sQuery(id+"F0.wireOp",EDGE,"E25.0"),sQuery(id+"F0.wireOp",EDGE,"E25.1"),sQuery(id+"F0.wireOp",EDGE,"E25.2"),sQuery(id+"F0.wireOp",EDGE,"E25.3"),sQuery(id+"F0.wireOp",EDGE,"E25.4"),sQuery(id+"F0.wireOp",EDGE,"E25.5"),sQuery(id+"F0.wireOp",EDGE,"E25.6"),sQuery(id+"F0.wireOp",EDGE,"E25.7")])],"isStart":false})})});
            extrude(context, id + "F13", {"entities" : qUnion([Q0]), "operationType" : NewBodyOperationType.REMOVE, "endBound" : BoundingType.UP_TO_SURFACE, "endBoundEntityFace" : qUnion([Q1]), "depth" : 25 * mm});
        }
        {
            var Q0;
            Q0=makeQuery(id+"F3.boolean.opBoolean","COPY",EDGE,{"derivedFrom":makeQuery(id+"F3.opExtrude","CAP_EDGE",EDGE,{"disambiguationData":[OSD([sQuery(id+"F0.wireOp",EDGE,"E25.6")])],"isStart":false})});
            var Q1;
            Q1=makeQuery(id+"F8.boolean.opBoolean","INTERSECT",EDGE,{"derivedFrom":[makeQuery(id+"F5.opExtrude","SWEPT_FACE",FACE,{"disambiguationData":[OSD([sQuery(id+"F4.wireOp",EDGE,"E30")])]}),makeQuery(id+"F8.opExtrude","CAP_FACE",FACE,{"disambiguationData":[OSD([sQuery(id+"F7.wireOp",EDGE,"E67")])],"isStart":false})]});
            var Q2;
            Q2=makeQuery(id+"F8.boolean.opBoolean","INTERSECT",EDGE,{"disambiguationData":[OD(1.0)],"derivedFrom":[makeQuery(id+"F5.opExtrude","SWEPT_FACE",FACE,{"disambiguationData":[OSD([sQuery(id+"F4.wireOp",EDGE,"E30")])]}),makeQuery(id+"F8.opExtrude","SWEPT_FACE",FACE,{"disambiguationData":[OSD([sQuery(id+"F7.wireOp",EDGE,"E67")])]})]});
            var Q3;
            {var subQ0=sQuery(id+"F4.wireOp",EDGE,"E30");Q3=makeQuery(id+"F8.boolean.opBoolean","SPLIT",EDGE,{"disambiguationData":[TD([makeQuery(id+"F5.opExtrude","SWEPT_FACE",FACE,{"disambiguationData":[OSD([sQuery(id+"F4.wireOp",EDGE,"E35.filletArc")])]})])],"derivedFrom":makeQuery(id+"F5.opExtrude","CAP_EDGE",EDGE,{"disambiguationData":[OSD([subQ0])],"isStart":false})});}
            var Q4;
            {var subQ0=sQuery(id+"F0.wireOp",EDGE,"E25.7");var subQ1=sQuery(id+"F0.wireOp",EDGE,"E25.1");var subQ2=sQuery(id+"F0.wireOp",EDGE,"E25.6");var subQ3=sQuery(id+"F0.wireOp",EDGE,"E25.5");var subQ4=sQuery(id+"F0.wireOp",EDGE,"E25.4");var subQ5=sQuery(id+"F0.wireOp",EDGE,"E25.0");var subQ6=sQuery(id+"F0.wireOp",EDGE,"E25.2");var subQ7=sQuery(id+"F0.wireOp",EDGE,"E25.3");Q4=makeQuery(id+"F8.boolean.opBoolean","INTERSECT",EDGE,{"derivedFrom":[makeQuery(id+"F5.boolean.opBoolean","SPLIT",FACE,{"disambiguationData":[TD([makeQuery(id+"F2.opExtrude","SWEPT_FACE",FACE,{"disambiguationData":[OSD([subQ5])]})])],"derivedFrom":makeQuery(id+"F3.boolean.opBoolean","COPY",FACE,{"derivedFrom":makeQuery(id+"F3.opExtrude","CAP_FACE",FACE,{"disambiguationData":[OSD([subQ5,subQ1,subQ6,subQ7,subQ4,subQ3,subQ2,subQ0])],"isStart":false})})}),makeQuery(id+"F8.opExtrude","SWEPT_FACE",FACE,{"disambiguationData":[OSD([sQuery(id+"F7.wireOp",EDGE,"E67")])]})]});}
            var Q5;
            Q5=makeQuery(id+"F8.boolean.opBoolean","INTERSECT",EDGE,{"disambiguationData":[OD(0.0)],"derivedFrom":[makeQuery(id+"F5.opExtrude","SWEPT_FACE",FACE,{"disambiguationData":[OSD([sQuery(id+"F4.wireOp",EDGE,"E30")])]}),makeQuery(id+"F8.opExtrude","SWEPT_FACE",FACE,{"disambiguationData":[OSD([sQuery(id+"F7.wireOp",EDGE,"E67")])]})]});
            fillet(context, id + "F14", {"entities" : qUnion([Q0, Q1, Q2, Q3, Q4, Q5]), "radius" : 3 * mm, "tangentPropagation" : true, "allowEdgeOverflow" : false});
        }
        {
            var Q0;
            Q0=makeQuery(id+"F1.opExtrude","CAP_EDGE",EDGE,{"disambiguationData":[OSD([sQuery(id+"F0.wireOp",EDGE,"E1.bottom")])],"isStart":false});
            fillet(context, id + "F15", {"entities" : qUnion([Q0]), "radius" : 2 * mm, "tangentPropagation" : true, "allowEdgeOverflow" : false});
        }
        {
            var Q0;
            {var subQ0=sQuery(id+"F0.wireOp",EDGE,"E21.filletArc");var subQ1=sQuery(id+"F0.wireOp",EDGE,"E7");var subQ2=sQuery(id+"F0.wireOp",EDGE,"E6");var subQ3=sQuery(id+"F0.wireOp",EDGE,"E5");var subQ4=sQuery(id+"F0.wireOp",EDGE,"E4");var subQ5=sQuery(id+"F0.wireOp",EDGE,"E22.filletArc");var subQ6=sQuery(id+"F0.wireOp",EDGE,"E1.bottom");var subQ7=sQuery(id+"F0.wireOp",EDGE,"E1.right");var subQ8=sQuery(id+"F0.wireOp",EDGE,"E1.top");var subQ9=sQuery(id+"F0.wireOp",EDGE,"E1.left");var subQ10=sQuery(id+"F0.wireOp",EDGE,"E23.filletArc");var subQ11=sQuery(id+"F0.wireOp",EDGE,"E24.filletArc");Q0=makeQuery(id+"F2.boolean.opBoolean","SPLIT",FACE,{"disambiguationData":[TD([makeQuery(id+"F1.opExtrude","SWEPT_FACE",FACE,{"disambiguationData":[OSD([subQ6])]})])],"derivedFrom":makeQuery(id+"F1.opExtrude","CAP_FACE",FACE,{"disambiguationData":[OSD([subQ6,subQ8,subQ9,subQ7,subQ4,subQ3,subQ2,subQ1,subQ0,subQ5,subQ10,subQ11])],"isStart":true})});}
            var sketch = newSketch(context, id + "F16", { "sketchPlane" : qUnion([Q0])});
            skLineSegment(sketch, "E79.0", {"start": v(-70, 90) * mm, "end": v(70, 90) * mm});
            skArc(sketch, "E79.1", {"start": v(-70, 90) * mm, "mid": v(-77.07, 87.07) * mm, "end": v(-80, 80) * mm});
            skLineSegment(sketch, "E79.2", {"start": v(-80, -80) * mm, "end": v(-80, 80) * mm});
            skArc(sketch, "E80.2", {"start": v(80, 80) * mm, "mid": v(77.07, 87.07) * mm, "end": v(70, 90) * mm});
            skLineSegment(sketch, "E80.3", {"start": v(80, -80) * mm, "end": v(80, 80) * mm});
            skArc(sketch, "E80.5", {"start": v(-80, -80) * mm, "mid": v(-77.07, -87.07) * mm, "end": v(-70, -90) * mm});
            skLineSegment(sketch, "E80.6", {"start": v(-70, -90) * mm, "end": v(70, -90) * mm});
            skArc(sketch, "E80.7", {"start": v(56.15, -48.18) * mm, "mid": v(58.99, -44.68) * mm, "end": v(60, -40.3) * mm});
            skArc(sketch, "E80.8", {"start": v(-56.15, -48.18) * mm, "mid": v(0, -67.5) * mm, "end": v(56.15, -48.18) * mm});
            skLineSegment(sketch, "E80.9", {"start": v(60, 40.3) * mm, "end": v(60, -40.3) * mm});
            skArc(sketch, "E80.10", {"start": v(56.15, 48.18) * mm, "mid": v(0, 67.5) * mm, "end": v(-56.15, 48.18) * mm});
            skLineSegment(sketch, "E80.11", {"start": v(-60, 40.3) * mm, "end": v(-60, -40.3) * mm});
            skArc(sketch, "E80.12", {"start": v(-56.15, 48.18) * mm, "mid": v(-58.99, 44.68) * mm, "end": v(-60, 40.3) * mm});
            skArc(sketch, "E80.13", {"start": v(-60, -40.3) * mm, "mid": v(-58.99, -44.68) * mm, "end": v(-56.15, -48.18) * mm});
            skArc(sketch, "E80.14", {"start": v(70, -90) * mm, "mid": v(77.07, -87.07) * mm, "end": v(80, -80) * mm});
            skArc(sketch, "E80.15", {"start": v(60, 40.3) * mm, "mid": v(58.99, 44.68) * mm, "end": v(56.15, 48.18) * mm});
            skCircle(sketch, "E80.16", {"center": v(60, -67.5) * mm, "radius": 4 * mm});
            skCircle(sketch, "E80.17", {"center": v(60, 67.5) * mm, "radius": 4 * mm});
            skCircle(sketch, "E80.18", {"center": v(-60, -67.5) * mm, "radius": 4 * mm});
            skLineSegment(sketch, "E81", {"start": v(-33, 90) * mm, "end": v(-15, 108) * mm});
            skLineSegment(sketch, "E82", {"start": v(-15, 108) * mm, "end": v(-15, 120) * mm});
            skLineSegment(sketch, "E83", {"start": v(33, 90) * mm, "end": v(15, 108) * mm});
            skLineSegment(sketch, "E84", {"start": v(15, 108) * mm, "end": v(15, 120) * mm});
            skArc(sketch, "E85", {"start": v(15, 120) * mm, "mid": v(0, 135) * mm, "end": v(-15, 120) * mm});
            skCircle(sketch, "E86", {"center": v(0, 120) * mm, "radius": 6 * mm});
            skLineSegment(sketch, "E87", {"start": v(0, 23.75) * mm, "end": v(0, 120) * mm, "construction": true});
            skLineSegment(sketch, "E88", {"start": v(80, 0) * mm, "end": v(-80, 0) * mm, "construction": true});
            skArc(sketch, "E89.MirrorCS", {"start": v(-15, 120) * mm, "mid": v(0, 135) * mm, "end": v(15, 120) * mm});
            skLineSegment(sketch, "E90.MirrorCS", {"start": v(-33, -90) * mm, "end": v(-15, -108) * mm});
            skLineSegment(sketch, "E91.MirrorCS", {"start": v(-15, -108) * mm, "end": v(-15, -120) * mm});
            skLineSegment(sketch, "E92.MirrorCS", {"start": v(33, -90) * mm, "end": v(15, -108) * mm});
            skLineSegment(sketch, "E93.MirrorCS", {"start": v(15, -108) * mm, "end": v(15, -120) * mm});
            skArc(sketch, "E94.MirrorCS", {"start": v(15, -120) * mm, "mid": v(0, -135) * mm, "end": v(-15, -120) * mm});
            skCircle(sketch, "E95.MirrorC", {"center": v(0, -120) * mm, "radius": 6 * mm});
            skArc(sketch, "E96.MirrorCS", {"start": v(-15, -120) * mm, "mid": v(0, -135) * mm, "end": v(15, -120) * mm});
            skLineSegment(sketch, "E97.MirrorCS", {"start": v(0, -23.75) * mm, "end": v(0, -120) * mm, "construction": true});
            skSolve(sketch);
        }
        {
            var Q0;
            Q0 = qSketchRegion(id + "F16", true);
            extrude(context, id + "F17", {"entities" : qUnion([Q0]), "depth" : 25 * mm, "offsetDistance" : 25 * mm});
        }
    });
